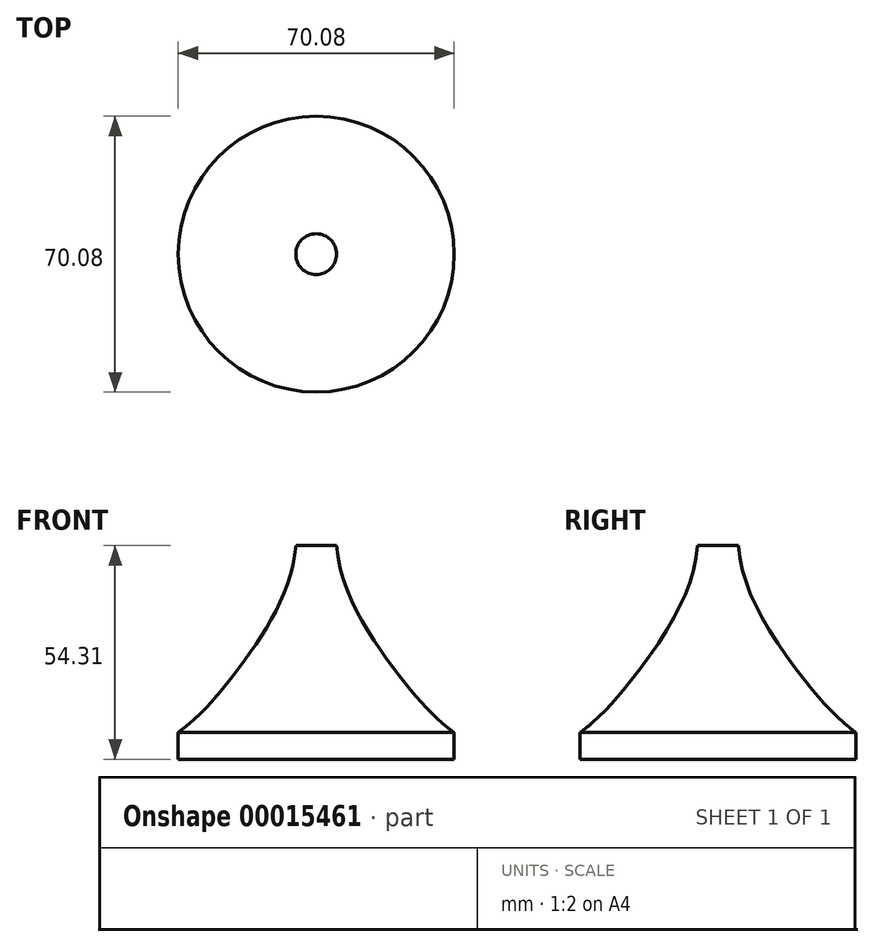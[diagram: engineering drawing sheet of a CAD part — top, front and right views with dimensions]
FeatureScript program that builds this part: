
annotation { "Feature Type Name" : "Feature", "Feature Type Description" : "" }
export const myFeature = defineFeature(function(context is Context, id is Id, definition is map)
    precondition{}
    {
        {
            var Q0;
            Q0=qCreatedBy(makeId("Front.planeOp"),FACE);
            var sketch = newSketch(context, id + "F0", { "sketchPlane" : qUnion([Q0])});
            skLineSegment(sketch, "E0", {"start": v(0, 54.3) * mm, "end": v(0, 0) * mm});
            skLineSegment(sketch, "E1", {"start": v(0, 54.3) * mm, "end": v(-5.18, 54.3) * mm});
            skFitSpline(sketch, "E2", {"points": [v(-5.18, 54.3) * mm, v(-21.7, 20.5) * mm, v(-35.04, 6.8) * mm], "startDerivative": vector(-4.29, -64.85) * mm, "endDerivative": vector(-35.38, -26.23) * mm});
            skLineSegment(sketch, "E3", {"start": v(-35.04, 6.8) * mm, "end": v(-35.04, 0) * mm});
            skLineSegment(sketch, "E4", {"start": v(-35.04, 0) * mm, "end": v(0, 0) * mm});
            skSolve(sketch);
        }
        {
            var Q0;
            Q0=makeQuery(id+"F0.imprint","IMPRINT",FACE,{"disambiguationData":[TD([[makeQuery(id+"F0.imprint","IMPRINT",EDGE,{"derivedFrom":sQuery(id+"F0.wireOp",EDGE,"E0")}),-1.0]])]});
            var Q1;
            Q1=sQuery(id+"F0.wireOp",EDGE,"E0");
            revolve(context, id + "F1", {"entities" : qUnion([Q0]), "axis" : qUnion([Q1]), "revolveType" : RevolveType.FULL});
        }
    });
